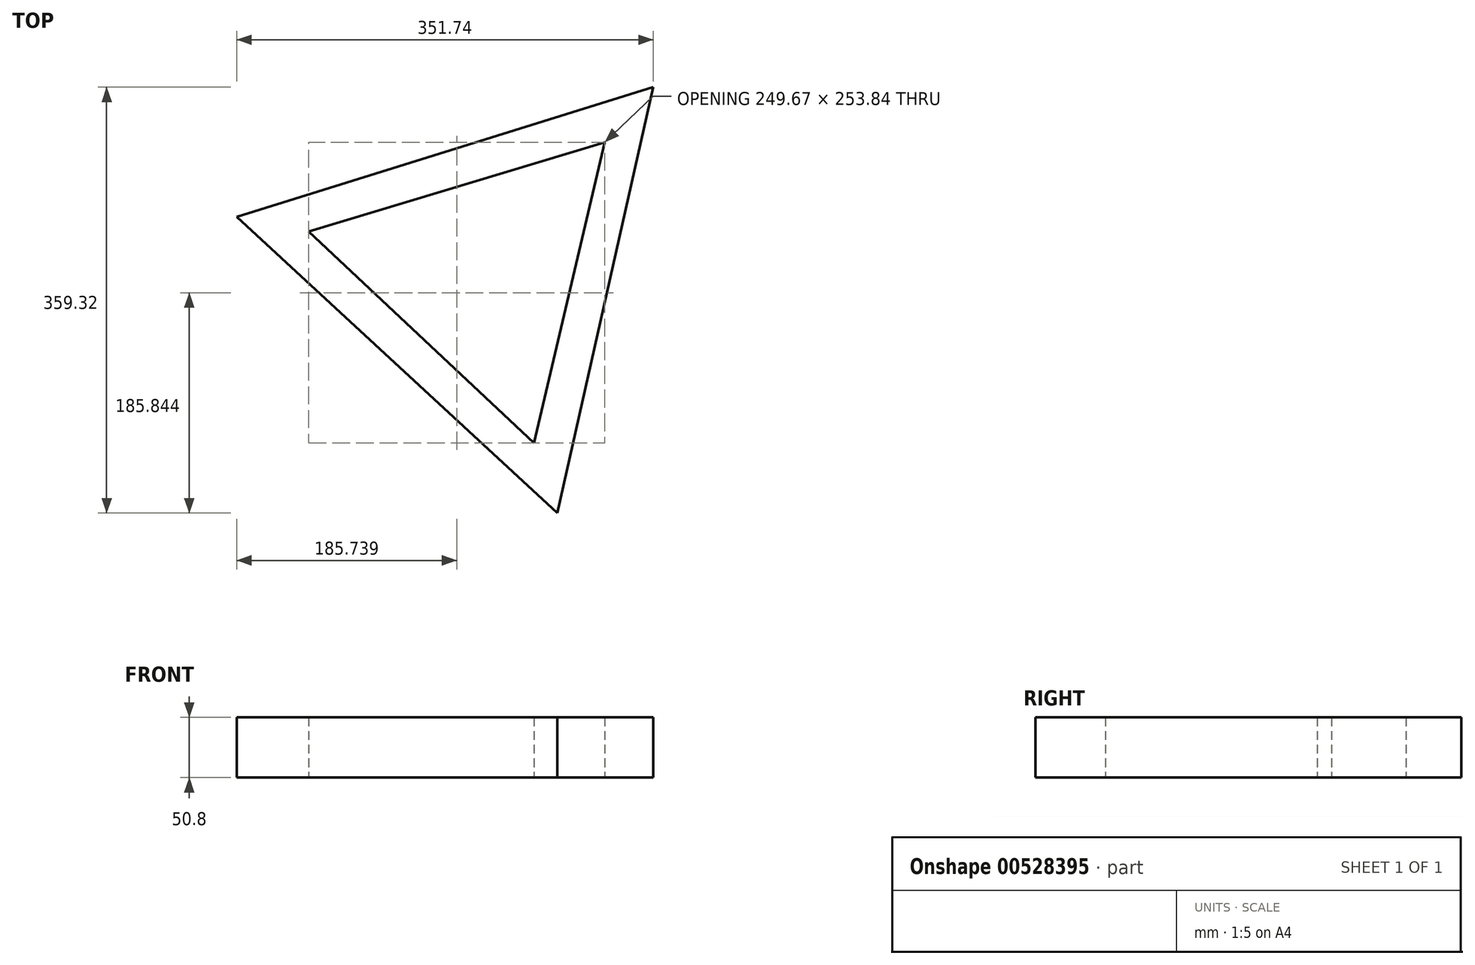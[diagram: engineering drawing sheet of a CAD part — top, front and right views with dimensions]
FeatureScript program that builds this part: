
annotation { "Feature Type Name" : "Feature", "Feature Type Description" : "" }
export const myFeature = defineFeature(function(context is Context, id is Id, definition is map)
    precondition{}
    {
        {
            var Q0;
            Q0=qCreatedBy(makeId("Top.planeOp"),FACE);
            var sketch = newSketch(context, id + "F0", { "sketchPlane" : qUnion([Q0])});
            skCircle(sketch, "E0.cCircle", {"center": v(0, 0) * mm, "radius": 106.34 * mm, "construction": true});
            skLineSegment(sketch, "E0.0", {"start": v(-207.46, 46.82) * mm, "end": v(144.28, 156.25) * mm});
            skLineSegment(sketch, "E0.1", {"start": v(144.28, 156.25) * mm, "end": v(63.18, -203.07) * mm});
            skLineSegment(sketch, "E0.2", {"start": v(63.18, -203.07) * mm, "end": v(-207.46, 46.82) * mm});
            skPoint(sketch, "E0.0.midPoint", {"position": v(-31.59, 101.54) * mm});
            skCircle(sketch, "E1.cCircle", {"center": v(0, 0) * mm, "radius": 75.28 * mm, "construction": true});
            skLineSegment(sketch, "E1.0", {"start": v(-146.56, 34.45) * mm, "end": v(103.11, 109.7) * mm});
            skLineSegment(sketch, "E1.1", {"start": v(103.11, 109.7) * mm, "end": v(43.44, -144.15) * mm});
            skLineSegment(sketch, "E1.2", {"start": v(43.44, -144.15) * mm, "end": v(-146.56, 34.45) * mm});
            skPoint(sketch, "E1.0.midPoint", {"position": v(-21.72, 72.07) * mm});
            skSolve(sketch);
        }
        {
            var Q0;
            Q0=makeQuery(id+"F0.imprint","IMPRINT",FACE,{"disambiguationData":[TD([[makeQuery(id+"F0.imprint","IMPRINT",EDGE,{"derivedFrom":sQuery(id+"F0.wireOp",EDGE,"E0.0")}),-1.0]])]});
            extrude(context, id + "F1", {"entities" : qUnion([Q0]), "depth" : 50.8 * mm, "offsetDistance" : 25.4 * mm});
        }
    });
